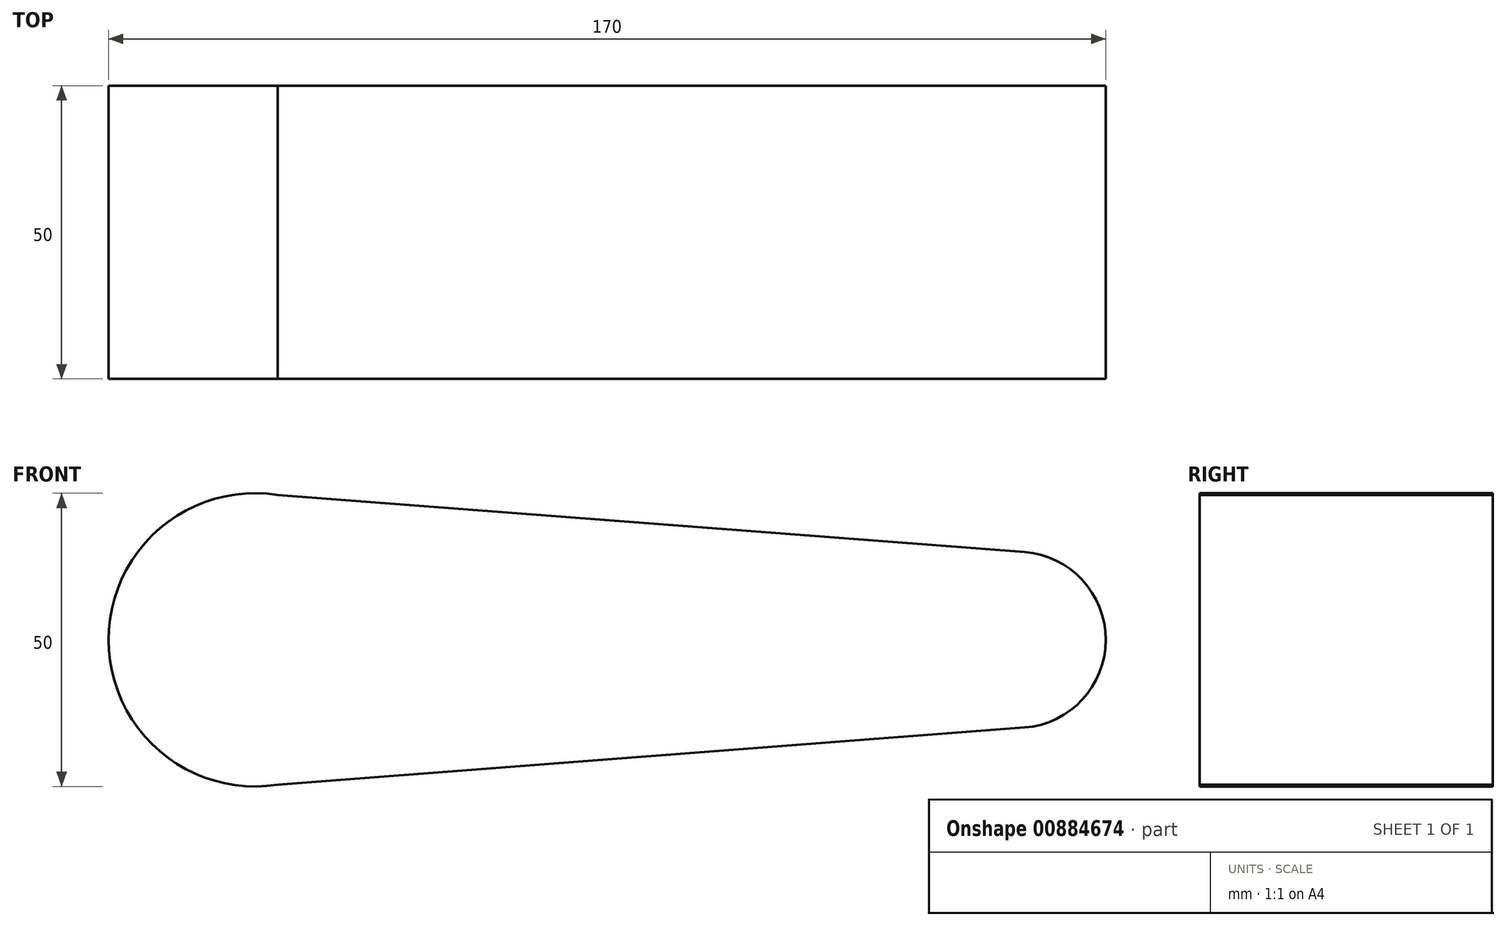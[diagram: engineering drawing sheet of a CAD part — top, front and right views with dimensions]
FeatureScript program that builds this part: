
annotation { "Feature Type Name" : "Feature", "Feature Type Description" : "" }
export const myFeature = defineFeature(function(context is Context, id is Id, definition is map)
    precondition{}
    {
        {
            var Q0;
            Q0=qCreatedBy(makeId("Front.planeOp"),FACE);
            var sketch = newSketch(context, id + "F0", { "sketchPlane" : qUnion([Q0])});
            skCircle(sketch, "E0", {"center": v(0, 0) * mm, "radius": 25 * mm});
            skCircle(sketch, "E1", {"center": v(130, 0) * mm, "radius": 15 * mm});
            skLineSegment(sketch, "E2", {"start": v(0, 25) * mm, "end": v(131.15, 14.96) * mm});
            skLineSegment(sketch, "E3", {"start": v(131.15, 14.96) * mm, "end": v(131.15, 14.96) * mm});
            skLineSegment(sketch, "E4", {"start": v(0, -25) * mm, "end": v(131.15, -14.96) * mm});
            skSolve(sketch);
        }
        {
            var Q0;
            Q0 = qSketchRegion(id + "F0", true);
            extrude(context, id + "F1", {"entities" : qUnion([Q0]), "depth" : 50 * mm, "offsetDistance" : 25 * mm});
        }
    });
